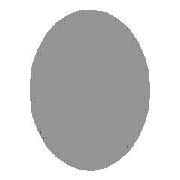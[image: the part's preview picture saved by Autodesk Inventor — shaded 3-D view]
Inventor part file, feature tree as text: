
AUTODESK INVENTOR PART (.ipt)
format: ipt  version: 2013 (Build 170138000, 138)  size: 110,080 bytes
history: native  units: mm (DEFAULTED — no unit token found)
features: other x4, sketch x3, plane x2, split x1
ambient origin geometry x8: Origin, YZ Plane, XZ Plane, XY Plane, X Axis, Y Axis, Z Axis, Center Point
bodies: Solid1 (feature_tree), Body (feature_tree)
feature tree (10):
  parser-record x1  (decoder bookkeeping rows leaked as tree rows — omitted from the tree; the rows remain in map.json)
  other  "Driven Length"
  other  "Start plane"
  other  "End plane"
  plane  "Work Plane4"
  split  "Split1"
  sketch  "Sketch"  dims[d2=0.0mm d4=-0.0mm d5=323.85mm d6=90.0deg d7=323.85mm]
  sketch  "Sketch2"  dims[d0=38.1mm]
  plane  "Work Plane3"
  sketch  "Sketch3"  dims[d1=323.85mm]
